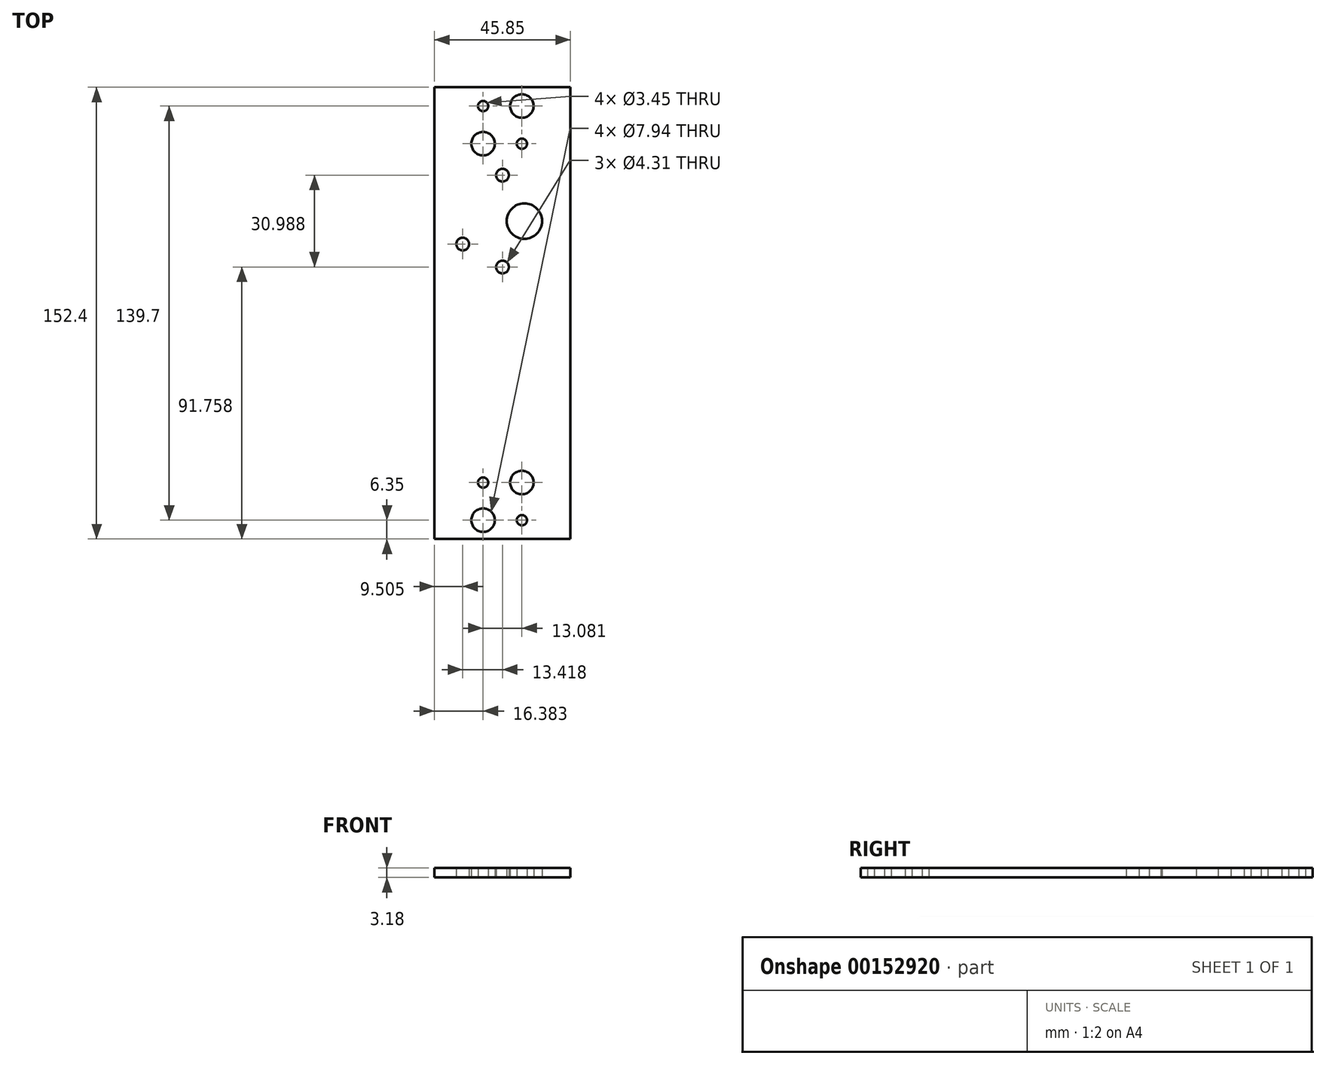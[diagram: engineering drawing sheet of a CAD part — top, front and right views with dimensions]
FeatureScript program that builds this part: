
annotation { "Feature Type Name" : "Feature", "Feature Type Description" : "" }
export const myFeature = defineFeature(function(context is Context, id is Id, definition is map)
    precondition{}
    {
        {
            var Q0;
            Q0=qCreatedBy(makeId("Top.planeOp"),FACE);
            var sketch = newSketch(context, id + "F0", { "sketchPlane" : qUnion([Q0])});
            skLineSegment(sketch, "E0.bottom", {"start": v(0, 0) * mm, "end": v(45.85, 0) * mm});
            skLineSegment(sketch, "E0.top", {"start": v(0, -152.4) * mm, "end": v(45.85, -152.4) * mm});
            skLineSegment(sketch, "E0.left", {"start": v(0, 0) * mm, "end": v(0, -152.4) * mm});
            skLineSegment(sketch, "E0.right", {"start": v(45.85, 0) * mm, "end": v(45.85, -152.4) * mm});
            skLineSegment(sketch, "E1", {"start": v(16.38, 0) * mm, "end": v(16.38, -6.35) * mm, "construction": true});
            skLineSegment(sketch, "E2", {"start": v(16.38, -6.35) * mm, "end": v(0, -6.35) * mm, "construction": true});
            skCircle(sketch, "E3", {"center": v(16.38, -6.35) * mm, "radius": 1.73 * mm});
            skLineSegment(sketch, "E4", {"start": v(16.38, -6.35) * mm, "end": v(16.38, -19.05) * mm, "construction": true});
            skCircle(sketch, "E5", {"center": v(16.38, -19.05) * mm, "radius": 3.97 * mm});
            skLineSegment(sketch, "E6", {"start": v(16.38, -152.4) * mm, "end": v(16.38, -146.05) * mm, "construction": true});
            skLineSegment(sketch, "E7", {"start": v(16.38, -146.05) * mm, "end": v(16.38, -133.35) * mm, "construction": true});
            skCircle(sketch, "E8", {"center": v(16.38, -133.35) * mm, "radius": 1.73 * mm});
            skCircle(sketch, "E9", {"center": v(16.38, -146.05) * mm, "radius": 3.97 * mm});
            skLineSegment(sketch, "E10", {"start": v(45.85, -6.35) * mm, "end": v(29.46, -6.35) * mm, "construction": true});
            skLineSegment(sketch, "E11", {"start": v(29.46, -6.35) * mm, "end": v(29.46, 0) * mm, "construction": true});
            skLineSegment(sketch, "E12", {"start": v(29.46, -6.35) * mm, "end": v(29.46, -19.05) * mm, "construction": true});
            skLineSegment(sketch, "E13", {"start": v(29.46, -152.4) * mm, "end": v(29.46, -146.05) * mm, "construction": true});
            skLineSegment(sketch, "E14", {"start": v(29.46, -146.05) * mm, "end": v(29.46, -133.35) * mm, "construction": true});
            skCircle(sketch, "E15", {"center": v(29.46, -6.35) * mm, "radius": 3.97 * mm});
            skCircle(sketch, "E16", {"center": v(29.46, -19.05) * mm, "radius": 1.73 * mm});
            skCircle(sketch, "E17", {"center": v(29.46, -133.35) * mm, "radius": 3.97 * mm});
            skCircle(sketch, "E18", {"center": v(29.46, -146.05) * mm, "radius": 1.73 * mm});
            skCircle(sketch, "E19", {"center": v(22.92, -45.15) * mm, "radius": 18.16 * mm, "construction": true});
            skCircle(sketch, "E20.cCircle", {"center": v(22.92, -45.15) * mm, "radius": 13.42 * mm, "construction": true});
            skLineSegment(sketch, "E20.0", {"start": v(36.34, -37.4) * mm, "end": v(36.34, -52.9) * mm, "construction": true});
            skLineSegment(sketch, "E20.1", {"start": v(36.34, -52.9) * mm, "end": v(22.92, -60.64) * mm, "construction": true});
            skLineSegment(sketch, "E20.2", {"start": v(22.92, -60.64) * mm, "end": v(9.5, -52.9) * mm, "construction": true});
            skLineSegment(sketch, "E20.3", {"start": v(9.5, -52.9) * mm, "end": v(9.5, -37.4) * mm, "construction": true});
            skLineSegment(sketch, "E20.4", {"start": v(9.5, -37.4) * mm, "end": v(22.92, -29.65) * mm, "construction": true});
            skLineSegment(sketch, "E20.5", {"start": v(22.92, -29.65) * mm, "end": v(36.34, -37.4) * mm, "construction": true});
            skPoint(sketch, "E20.0.midPoint", {"position": v(36.34, -45.15) * mm});
            skCircle(sketch, "E21", {"center": v(9.5, -52.9) * mm, "radius": 2.15 * mm});
            skCircle(sketch, "E22", {"center": v(22.92, -60.64) * mm, "radius": 2.15 * mm});
            skCircle(sketch, "E23", {"center": v(22.92, -29.65) * mm, "radius": 2.15 * mm});
            skLineSegment(sketch, "E24", {"start": v(22.92, -45.15) * mm, "end": v(30.29, -45.15) * mm, "construction": true});
            skCircle(sketch, "E25", {"center": v(30.29, -45.15) * mm, "radius": 5.97 * mm});
            skLineSegment(sketch, "E26", {"start": v(30.29, -45.15) * mm, "end": v(41.08, -45.15) * mm, "construction": true});
            skLineSegment(sketch, "E27", {"start": v(41.08, -45.15) * mm, "end": v(45.85, -45.15) * mm, "construction": true});
            skLineSegment(sketch, "E28", {"start": v(29.46, -19.05) * mm, "end": v(23.11, -19.05) * mm, "construction": true});
            skLineSegment(sketch, "E29", {"start": v(23.11, -19.05) * mm, "end": v(23.11, -26.99) * mm, "construction": true});
            skLineSegment(sketch, "E30", {"start": v(22.92, -45.15) * mm, "end": v(4.76, -45.15) * mm, "construction": true});
            skLineSegment(sketch, "E31", {"start": v(4.76, -45.15) * mm, "end": v(0, -45.15) * mm, "construction": true});
            skSolve(sketch);
        }
        {
            var Q0;
            Q0=makeQuery(id+"F0.imprint","IMPRINT",FACE,{"disambiguationData":[TD([[makeQuery(id+"F0.imprint","IMPRINT",EDGE,{"derivedFrom":sQuery(id+"F0.wireOp",EDGE,"E0.bottom")}),-1.0]])]});
            extrude(context, id + "F1", {"entities" : qUnion([Q0]), "depth" : 3.17 * mm});
        }
    });
